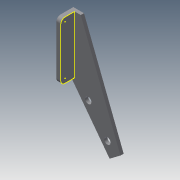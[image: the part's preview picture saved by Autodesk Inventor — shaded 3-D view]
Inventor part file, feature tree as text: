
AUTODESK INVENTOR PART (.ipt)
format: ipt  version: 2015 (Build 190159000, 159)  size: 163,840 bytes
history: native  units: mm
features: sketch x16, extrude x8, fillet x2
ambient origin geometry x8: Origin, YZ Plane, XZ Plane, XY Plane, X Axis, Y Axis, Z Axis, Center Point
bodies: Solid1 (feature_tree)
feature tree (26):
  sketch  "Sketch1"  dims[d4=3.0mm d5=3.0mm d6=2.0mm d7=0.0mm]
  extrude  "Extrusion1"  Depth=2.0mm TaperAngle=0.0deg
  extrude  "Extrusion2"  Depth=2.0mm TaperAngle=0.0deg
  extrude  "Extrusion3"  Depth=2.0mm TaperAngle=0.0deg
  sketch  "Sketch5"  dims[d19=0.5mm d20=0.0mm d21=10.0mm]
  extrude  "Extrusion4"  Depth=2.0mm TaperAngle=0.0deg
  sketch  "Sketch7"  dims[d25=1.5mm d26=0.0mm d27=10.0mm d28=0.0mm]
  sketch  "Sketch8"  dims[d29=2.0mm d30=2.0mm]
  extrude  "Extrusion5"  Depth=10.0mm
  sketch  "Sketch10"
  extrude  "Extrusion6"  Depth=1.5mm TaperAngle=0.0deg
  extrude  "Extrusion7"  Depth=10.0mm TaperAngle=0.0deg
  extrude  "Extrusion8"  Depth=2.0mm
  fillet  "Fillet1"  [1 undecoded]
  fillet  "Fillet2"  [1 undecoded]
  sketch  "Sketch14"
  sketch  "Sketch15"
  sketch  "Sketch16"
  sketch  "Sketch2"  dims[d8=10.0mm d11=2.0mm d12=0.0mm]
  sketch  "Sketch3"  dims[d13=5.0mm d14=2.0mm d15=0.0mm]
  sketch  "Sketch4"  dims[d16=2.0mm d17=6.0mm d18=0.0mm]
  sketch  "Sketch6"  dims[d22=5.0mm d23=1.5mm d24=0.0mm]
  sketch  "Sketch9"
  sketch  "Sketch11"
  sketch  "Sketch12"
  sketch  "Sketch13"
note: 2 required parameter values undecoded (feature->parameter linkage not recoverable at this tier; creation-order binding heuristic only, values carry confidence <= 0.55)
